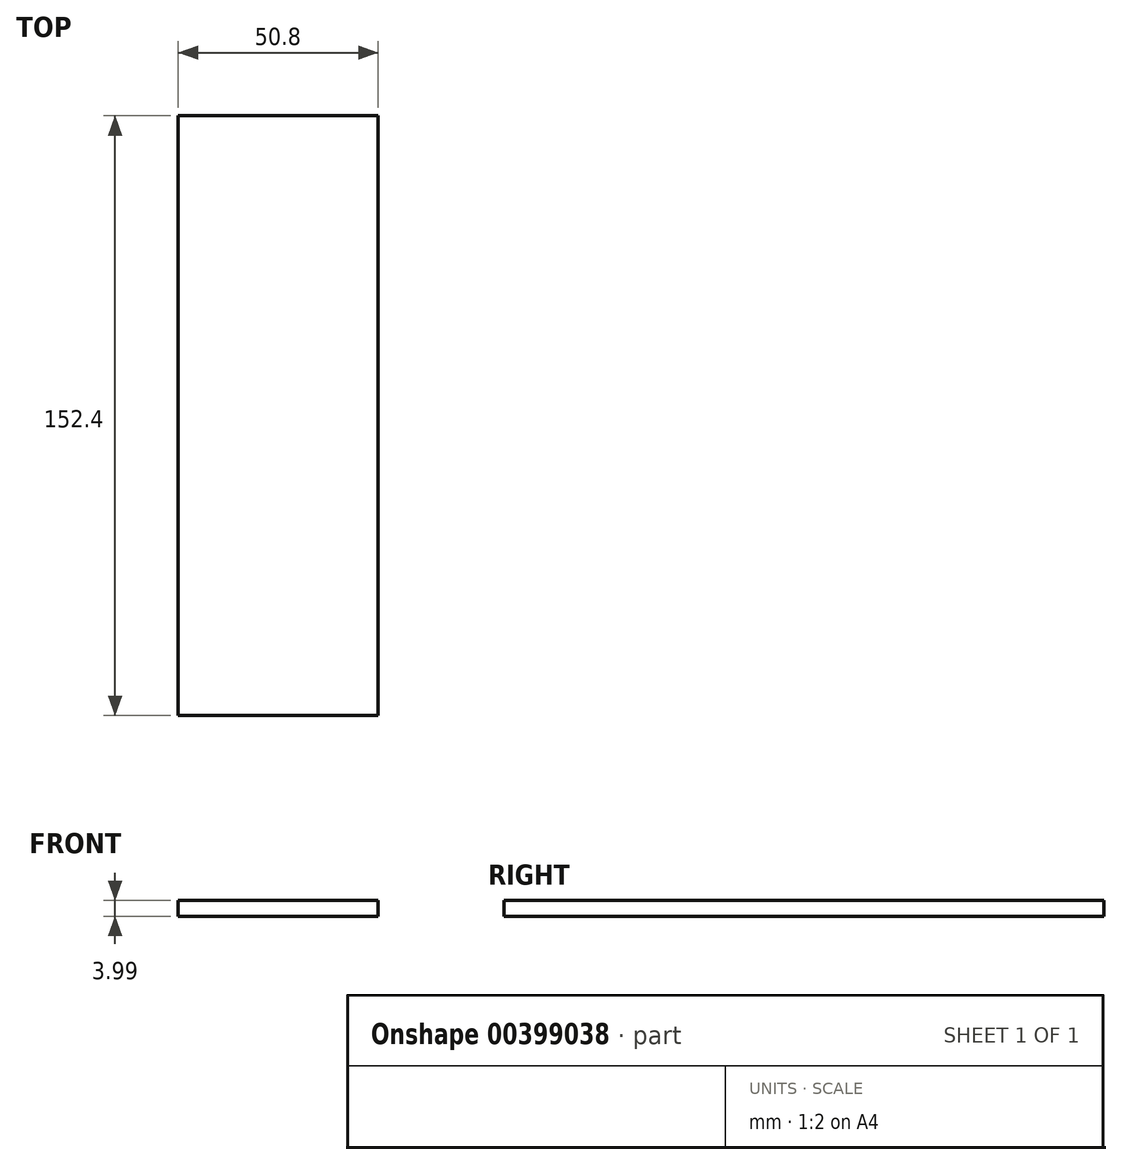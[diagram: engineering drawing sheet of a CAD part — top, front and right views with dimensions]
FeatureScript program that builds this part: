
annotation { "Feature Type Name" : "Feature", "Feature Type Description" : "" }
export const myFeature = defineFeature(function(context is Context, id is Id, definition is map)
    precondition{}
    {
        {
            var Q0;
            Q0=qCreatedBy(makeId("Top.planeOp"),FACE);
            var sketch = newSketch(context, id + "F0", { "sketchPlane" : qUnion([Q0])});
            skLineSegment(sketch, "E0.bottom", {"start": v(25.4, -76.2) * mm, "end": v(-25.4, -76.2) * mm});
            skLineSegment(sketch, "E0.top", {"start": v(25.4, 76.2) * mm, "end": v(-25.4, 76.2) * mm});
            skLineSegment(sketch, "E0.left", {"start": v(25.4, -76.2) * mm, "end": v(25.4, 76.2) * mm});
            skLineSegment(sketch, "E0.right", {"start": v(-25.4, -76.2) * mm, "end": v(-25.4, 76.2) * mm});
            skPoint(sketch, "E0.middle", {"position": v(0, 0) * mm});
            skSolve(sketch);
        }
        {
            var Q0;
            Q0 = qSketchRegion(id + "F0", true);
            extrude(context, id + "F1", {"entities" : qUnion([Q0]), "depth" : 4 * mm});
        }
    });
